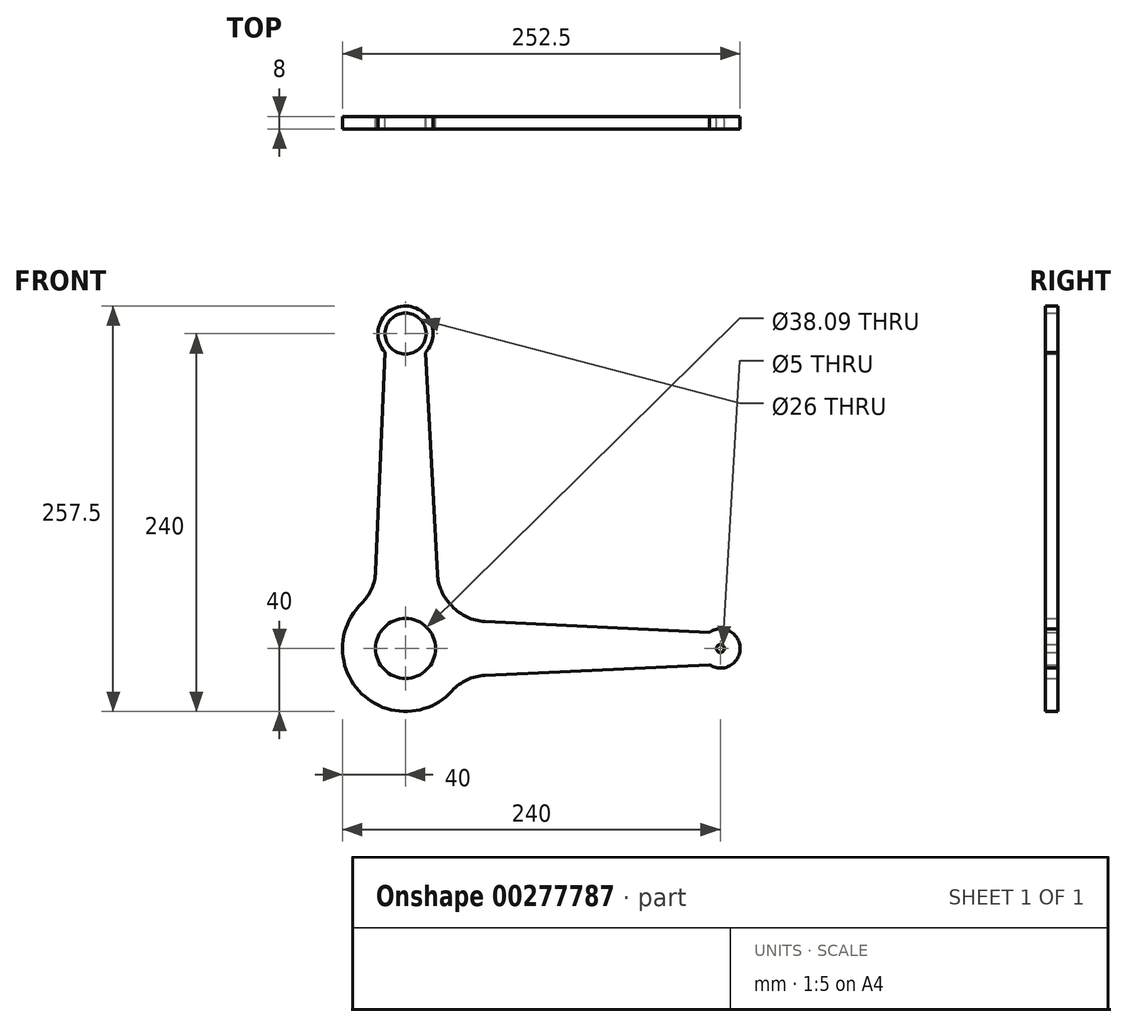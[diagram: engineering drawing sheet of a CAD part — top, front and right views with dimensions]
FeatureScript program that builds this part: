
annotation { "Feature Type Name" : "Feature", "Feature Type Description" : "" }
export const myFeature = defineFeature(function(context is Context, id is Id, definition is map)
    precondition{}
    {
        {
            var Q0;
            Q0=qCreatedBy(makeId("Front.planeOp"),FACE);
            var sketch = newSketch(context, id + "F0", { "sketchPlane" : qUnion([Q0])});
            skCircle(sketch, "E0", {"center": v(0, 0) * mm, "radius": 40 * mm});
            skCircle(sketch, "E1", {"center": v(0, 200) * mm, "radius": 17.5 * mm});
            skCircle(sketch, "E2", {"center": v(200, 0) * mm, "radius": 12.5 * mm});
            skLineSegment(sketch, "E3", {"start": v(-13.02, 188.3) * mm, "end": v(-19.54, 34.9) * mm});
            skLineSegment(sketch, "E4", {"start": v(12.63, 187.88) * mm, "end": v(21, 34.04) * mm});
            skLineSegment(sketch, "E5", {"start": v(192.95, -10.32) * mm, "end": v(35.81, -17.81) * mm});
            skLineSegment(sketch, "E6", {"start": v(192.96, 10.33) * mm, "end": v(35.81, 17.82) * mm});
            skCircle(sketch, "E7", {"center": v(0, 200) * mm, "radius": 13 * mm});
            skCircle(sketch, "E8", {"center": v(0, 0) * mm, "radius": 19.05 * mm});
            skCircle(sketch, "E9", {"center": v(200, 0) * mm, "radius": 2.5 * mm});
            skSolve(sketch);
        }
        {
            var Q0;
            {var subQ0=sQuery(id+"F0.wireOp",EDGE,"E3");Q0=makeQuery(id+"F0.imprint","IMPRINT",FACE,{"disambiguationData":[TD([[makeQuery(id+"F0.imprint","IMPRINT",EDGE,{"derivedFrom":subQ0}),1.0]])]});}
            var Q1;
            {var subQ0=sQuery(id+"F0.wireOp",EDGE,"E5");Q1=makeQuery(id+"F0.imprint","IMPRINT",FACE,{"disambiguationData":[TD([[makeQuery(id+"F0.imprint","IMPRINT",EDGE,{"derivedFrom":subQ0}),-1.0]])]});}
            var Q2;
            Q2=makeQuery(id+"F0.imprint","IMPRINT",FACE,{"disambiguationData":[TD([[makeQuery(id+"F0.imprint","IMPRINT",EDGE,{"derivedFrom":sQuery(id+"F0.wireOp",EDGE,"E8")}),-1.0]])]});
            var Q3;
            Q3=makeQuery(id+"F0.imprint","IMPRINT",FACE,{"disambiguationData":[TD([[makeQuery(id+"F0.imprint","IMPRINT",EDGE,{"derivedFrom":sQuery(id+"F0.wireOp",EDGE,"E7")}),-1.0]])]});
            var Q4;
            Q4=makeQuery(id+"F0.imprint","IMPRINT",FACE,{"disambiguationData":[TD([[makeQuery(id+"F0.imprint","IMPRINT",EDGE,{"derivedFrom":sQuery(id+"F0.wireOp",EDGE,"E9")}),-1.0]])]});
            extrude(context, id + "F1", {"entities" : qUnion([Q0, Q1, Q2, Q3, Q4]), "endBound" : BoundingType.SYMMETRIC, "depth" : 8 * mm});
        }
        {
            var Q0;
            Q0=makeQuery(id+"F1.opExtrude","SWEPT_EDGE",EDGE,{"disambiguationData":[OSD([sQuery(id+"F0.wireOp",EDGE,"E0"),sQuery(id+"F0.wireOp",EDGE,"E6")])]});
            fillet(context, id + "F2", {"entities" : qUnion([Q0]), "radius" : 30 * mm, "tangentPropagation" : true, "allowEdgeOverflow" : false});
        }
        {
            var Q0;
            Q0=makeQuery(id+"F1.opExtrude","SWEPT_EDGE",EDGE,{"disambiguationData":[OSD([sQuery(id+"F0.wireOp",EDGE,"E0"),sQuery(id+"F0.wireOp",EDGE,"E4")])]});
            fillet(context, id + "F3", {"entities" : qUnion([Q0]), "radius" : 30 * mm, "tangentPropagation" : true, "allowEdgeOverflow" : false});
        }
        {
            var Q0;
            Q0=makeQuery(id+"F1.opExtrude","SWEPT_EDGE",EDGE,{"disambiguationData":[OSD([sQuery(id+"F0.wireOp",EDGE,"E0"),sQuery(id+"F0.wireOp",EDGE,"E3")])]});
            fillet(context, id + "F4", {"entities" : qUnion([Q0]), "radius" : 30 * mm, "tangentPropagation" : true, "allowEdgeOverflow" : false});
        }
        {
            var Q0;
            Q0=makeQuery(id+"F1.opExtrude","SWEPT_EDGE",EDGE,{"disambiguationData":[OSD([sQuery(id+"F0.wireOp",EDGE,"E0"),sQuery(id+"F0.wireOp",EDGE,"E5")])]});
            fillet(context, id + "F5", {"entities" : qUnion([Q0]), "radius" : 30 * mm, "tangentPropagation" : true, "allowEdgeOverflow" : false});
        }
    });
